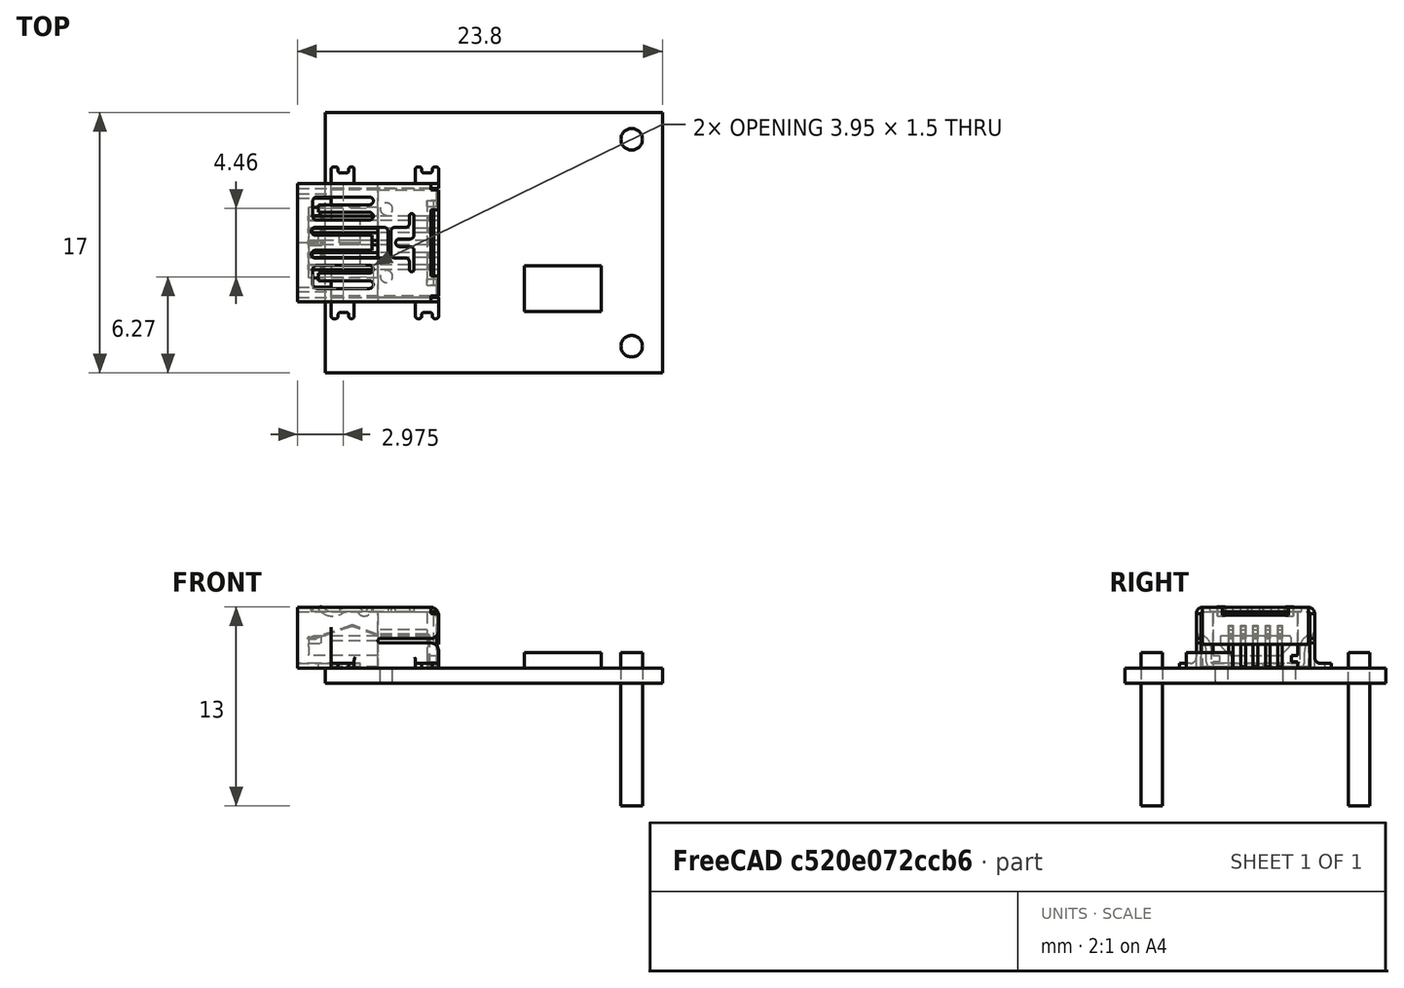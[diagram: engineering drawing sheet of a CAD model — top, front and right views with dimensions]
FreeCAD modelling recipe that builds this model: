
FCSTD DOCUMENT  (FreeCAD 0.16R)
Label: cargador
License: All rights reserved
LicenseURL: http://en.wikipedia.org/wiki/All_rights_reserved
objects: Part::Mirroring×3, Part::Box×2, Part::Cylinder×1, Part::Feature×1
note: 7 computed .brp shape members not serialized (recipe doc carries the construction recipe); baked Part::Feature solids carry a one-line shape summary decoded from their .brp

FEATURE [Part::Box] Box  label="Cubo"
  Height = 1
  Length = 22
  Width = 17
FEATURE [Part::Cylinder] Cylinder  label="Cilindro"
  Angle = 360
  Height = 10
  Placement = pos=(2,1.75,-8) rot=(0,0,1;0rad)
  Radius = 0.7
FEATURE [Part::Mirroring] Part__Mirroring  label="Cilindro (Mirror #1)"
  Base = (0,0,0)
  Normal = (0,0,1)
  Placement = pos=(0,13.5,-6) rot=(0,0,1;0rad)
  Source = -> Cylinder
FEATURE [Part::Mirroring] Part__Mirroring001  label="Cilindro (Mirror #2)"
  Base = (0,0,0)
  Normal = (0,0,1)
  Placement = pos=(18,0,-6) rot=(0,0,1;0rad)
  Source = -> Cylinder
FEATURE [Part::Mirroring] Part__Mirroring002  label="Cilindro (Mirror #3)"
  Base = (0,0,0)
  Normal = (0,0,1)
  Placement = pos=(18,0,-6) rot=(0,0,1;0rad)
  Source = -> Part__Mirroring
FEATURE [Part::Feature] USB_Mini_B_Lumberg_2486_01_Horizontal
  Placement = pos=(4,8.5,1) rot=(0,0,-1;1.5708rad)
  shape: bbox 9.2 x 9.9 x 4.997 mm, 472 faces (baked)
FEATURE [Part::Box] Box001  label="Cubo001"
  Height = 1
  Length = 5
  Placement = pos=(13,4,1) rot=(0,0,1;0rad)
  Width = 3
